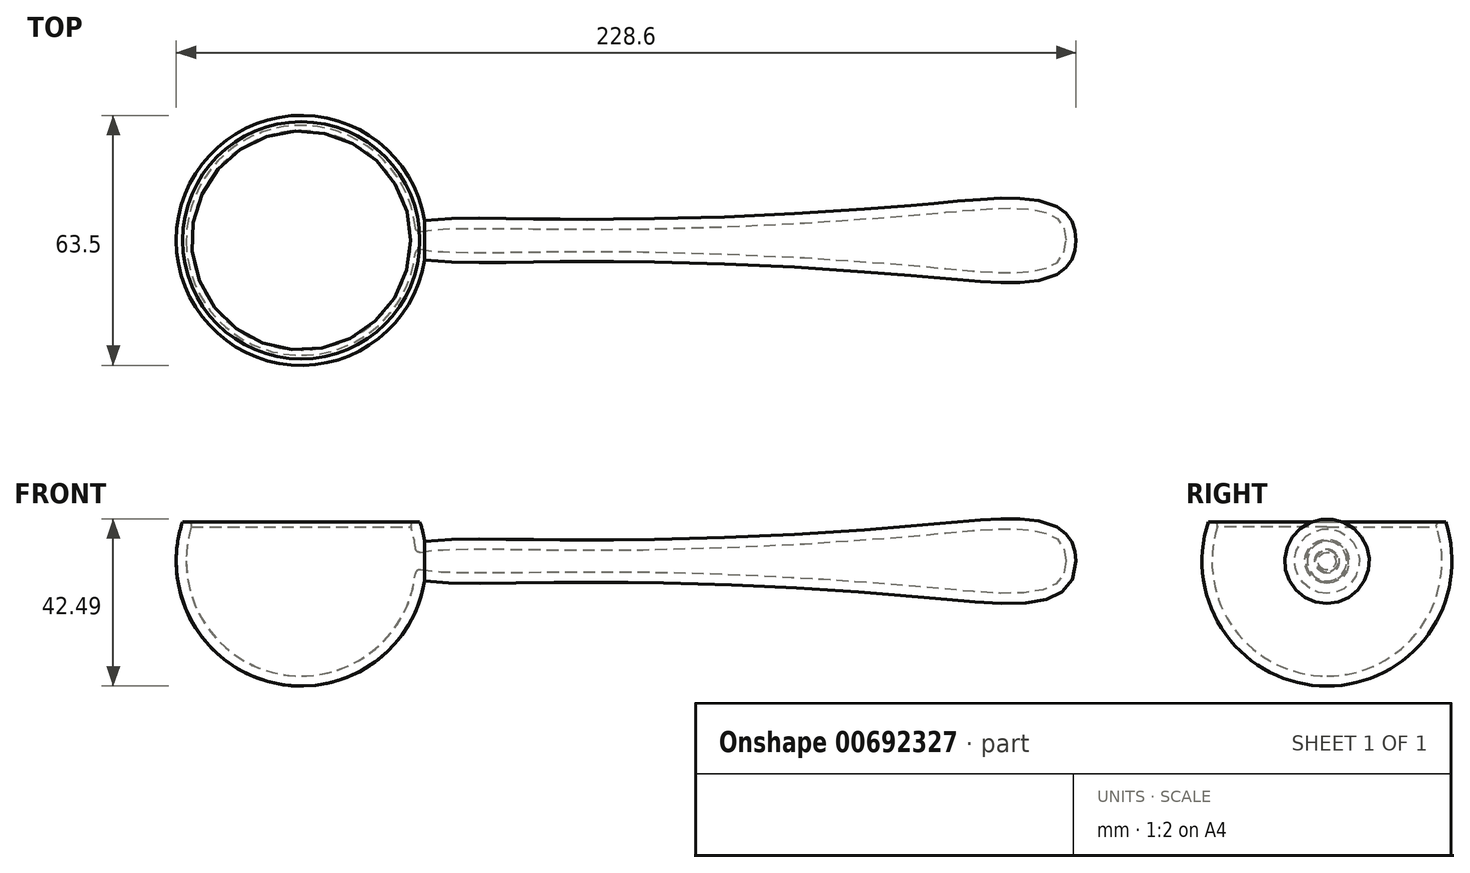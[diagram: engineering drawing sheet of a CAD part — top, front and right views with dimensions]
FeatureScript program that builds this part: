
annotation { "Feature Type Name" : "Feature", "Feature Type Description" : "" }
export const myFeature = defineFeature(function(context is Context, id is Id, definition is map)
    precondition{}
    {
        {
            var Q0;
            Q0=qCreatedBy(makeId("Front.planeOp"),FACE);
            var sketch = newSketch(context, id + "F0", { "sketchPlane" : qUnion([Q0])});
            skFitSpline(sketch, "E0", {"points": [v(196.85, 0) * mm, v(163.48, -9.66) * mm, v(63.55, -5.41) * mm, v(31.75, 0) * mm], "startDerivative": vector(0, -142.77) * mm, "endDerivative": vector(159.66, 76.37) * mm});
            skArc(sketch, "E1", {"start": v(-31.75, 0) * mm, "mid": v(-2.5, -31.65) * mm, "end": v(31.35, -5) * mm});
            skLineSegment(sketch, "E2", {"start": v(31.75, 0) * mm, "end": v(196.85, 0) * mm});
            skLineSegment(sketch, "E3", {"start": v(31.75, 0) * mm, "end": v(31.75, 0) * mm});
            skLineSegment(sketch, "E4", {"start": v(31.75, 0) * mm, "end": v(-31.75, 0) * mm});
            skPoint(sketch, "E5.trimOffspring.end.orphan", {"position": v(-31.75, 0) * mm});
            skLineSegment(sketch, "E6", {"start": v(-31.75, 0) * mm, "end": v(-112, 0) * mm, "construction": true});
            skSolve(sketch);
        }
        {
            var Q0;
            Q0 = qSketchRegion(id + "F0", true);
            var Q1;
            Q1=sQuery(id+"F0.wireOp",EDGE,"E6");
            revolve(context, id + "F1", {"entities" : qUnion([Q0]), "axis" : qUnion([Q1]), "revolveType" : RevolveType.FULL});
        }
        {
            var Q0;
            Q0=qCreatedBy(makeId("Front.planeOp"),FACE);
            var sketch = newSketch(context, id + "F2", { "sketchPlane" : qUnion([Q0])});
            skLineSegment(sketch, "E7.bottom", {"start": v(-46.75, 40.15) * mm, "end": v(39.48, 40.15) * mm});
            skLineSegment(sketch, "E7.top", {"start": v(-46.75, 10) * mm, "end": v(39.48, 10) * mm});
            skLineSegment(sketch, "E7.left", {"start": v(-46.75, 40.15) * mm, "end": v(-46.75, 10) * mm});
            skLineSegment(sketch, "E7.right", {"start": v(39.48, 40.15) * mm, "end": v(39.48, 10) * mm});
            skSolve(sketch);
        }
        {
            var Q0;
            Q0 = qSketchRegion(id + "F2", true);
            extrude(context, id + "F3", {"entities" : qUnion([Q0]), "operationType" : NewBodyOperationType.REMOVE, "endBound" : BoundingType.UP_TO_NEXT, "depth" : 25 * mm, "offsetDistance" : 25 * mm, "hasSecondDirection" : true, "secondDirectionBound" : SecondDirectionBoundingType.THROUGH_ALL, "secondDirectionOppositeDirection" : true, "secondDirectionDepth" : 25 * mm});
        }
        {
            var Q0;
            Q0=makeQuery(id+"F3.boolean.opBoolean","COPY",FACE,{"derivedFrom":makeQuery(id+"F3.opExtrude","SWEPT_FACE",FACE,{"disambiguationData":[OSD([sQuery(id+"F2.wireOp",EDGE,"E7.top")])]})});
            shell(context, id + "F4", {"entities" : qUnion([Q0]), "thickness" : 2.54 * mm});
        }
        {
            var Q0;
            Q0=makeQuery(id+"F8kBHhC0nLzrK5p_0.boolean.opBoolean","INTERSECT",EDGE,{"derivedFrom":[makeQuery(id+"F1.opRevolve","SWEPT_FACE",FACE,{"disambiguationData":[OSD([sQuery(id+"F0.wireOp",EDGE,"E1")])]}),makeQuery(id+"F8kBHhC0nLzrK5p_0.opExtrude","SWEPT_FACE",FACE,{"disambiguationData":[OSD([sQuery(id+"F0.wireOp",EDGE,"E4")])]})]});
            var Q1;
            Q1=makeQuery(id+"F4.opShell","OFFSET_EDGE",EDGE,{"disambiguationData":[OSD([sQuery(id+"F0.wireOp",EDGE,"E1"),sQuery(id+"F0.wireOp",EDGE,"E4")])]});
            fillet(context, id + "F5", {"entities" : qUnion([Q0, Q1]), "radius" : 1 * mm, "tangentPropagation" : true, "allowEdgeOverflow" : false});
        }
    });
